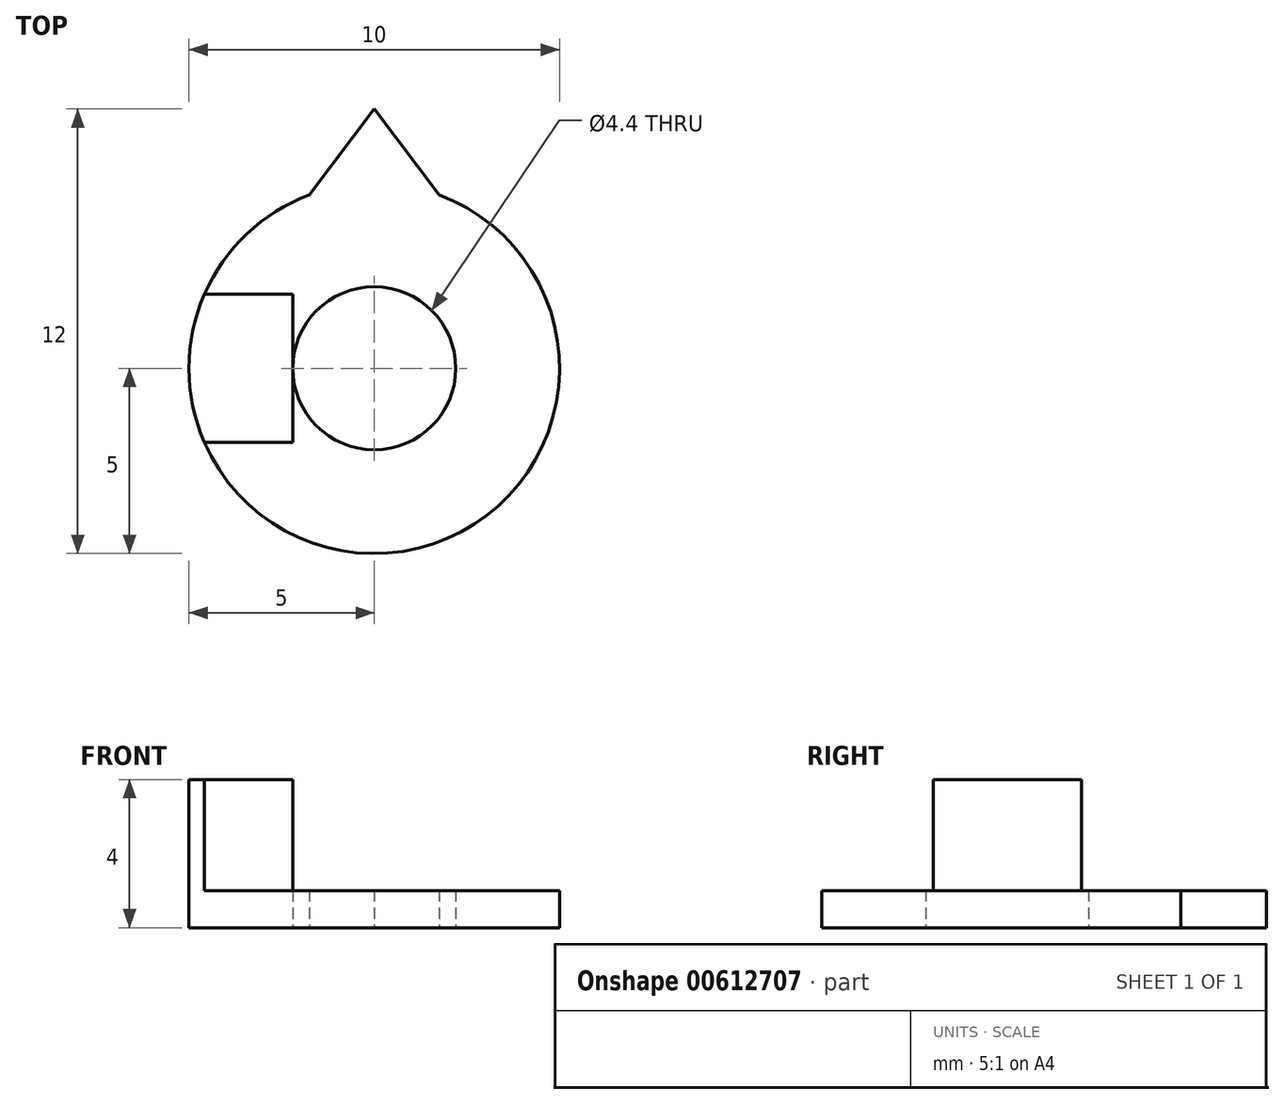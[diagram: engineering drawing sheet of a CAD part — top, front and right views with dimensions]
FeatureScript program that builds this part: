
annotation { "Feature Type Name" : "Feature", "Feature Type Description" : "" }
export const myFeature = defineFeature(function(context is Context, id is Id, definition is map)
    precondition{}
    {
        {
            var Q0;
            Q0=qCreatedBy(makeId("Top.planeOp"),FACE);
            var sketch = newSketch(context, id + "F0", { "sketchPlane" : qUnion([Q0])});
            skCircle(sketch, "E0", {"center": v(0, 0) * mm, "radius": 2.2 * mm});
            skCircle(sketch, "E1", {"center": v(0, 0) * mm, "radius": 5 * mm});
            skLineSegment(sketch, "E2", {"start": v(-1.75, 4.68) * mm, "end": v(0, 7) * mm});
            skLineSegment(sketch, "E3", {"start": v(0, 7) * mm, "end": v(1.75, 4.68) * mm});
            skSolve(sketch);
        }
        {
            var Q0;
            Q0=makeQuery(id+"F0.imprint","IMPRINT",FACE,{"disambiguationData":[TD([[makeQuery(id+"F0.imprint","IMPRINT",EDGE,{"derivedFrom":sQuery(id+"F0.wireOp",EDGE,"E0")}),-1.0]])]});
            var Q1;
            {var subQ0=sQuery(id+"F0.wireOp",EDGE,"E2");Q1=makeQuery(id+"F0.imprint","IMPRINT",FACE,{"disambiguationData":[TD([[makeQuery(id+"F0.imprint","IMPRINT",EDGE,{"derivedFrom":subQ0}),-1.0]])]});}
            extrude(context, id + "F1", {"entities" : qUnion([Q0, Q1]), "depth" : 1 * mm, "offsetDistance" : 25 * mm});
        }
        {
            var Q0;
            Q0=makeQuery(id+"F1.opExtrude","CAP_FACE",FACE,{"disambiguationData":[OSD([sQuery(id+"F0.wireOp",EDGE,"E0"),sQuery(id+"F0.wireOp",EDGE,"E1"),sQuery(id+"F0.wireOp",EDGE,"E2"),sQuery(id+"F0.wireOp",EDGE,"E3")])],"isStart":false});
            var sketch = newSketch(context, id + "F2", { "sketchPlane" : qUnion([Q0])});
            skLineSegment(sketch, "E4", {"start": v(-4.58, 2) * mm, "end": v(-2.2, 2) * mm});
            skLineSegment(sketch, "E5", {"start": v(-4.58, -2) * mm, "end": v(-2.2, -2) * mm});
            skArc(sketch, "E6", {"start": v(-4.58, 2) * mm, "mid": v(-5, 0) * mm, "end": v(-4.58, -2) * mm});
            skLineSegment(sketch, "E7", {"start": v(-2.2, 2) * mm, "end": v(0, 0) * mm, "construction": true});
            skLineSegment(sketch, "E8", {"start": v(-2.2, -2) * mm, "end": v(0, 0) * mm, "construction": true});
            skLineSegment(sketch, "E9", {"start": v(-2.2, 2) * mm, "end": v(-2.2, -2) * mm});
            skSolve(sketch);
        }
        {
            var Q0;
            Q0=qSketchRegion(id+"F2",true);
            extrude(context, id + "F3", {"entities" : qUnion([Q0]), "operationType" : NewBodyOperationType.ADD, "depth" : 3 * mm, "offsetDistance" : 25 * mm});
        }
    });
